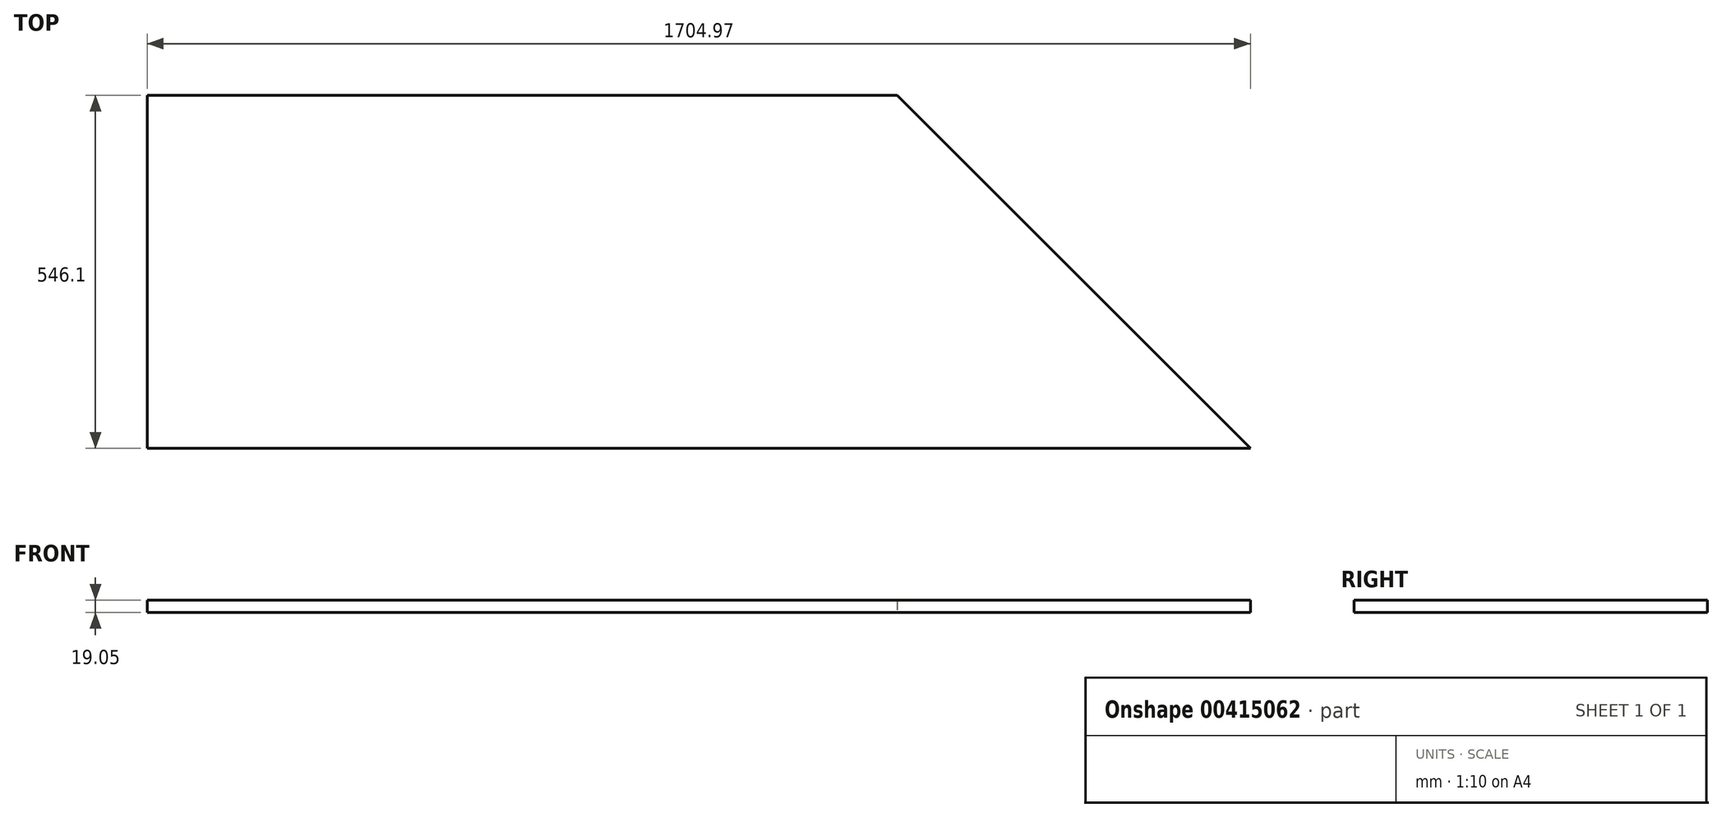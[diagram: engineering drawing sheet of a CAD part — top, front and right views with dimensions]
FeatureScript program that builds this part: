
annotation { "Feature Type Name" : "Feature", "Feature Type Description" : "" }
export const myFeature = defineFeature(function(context is Context, id is Id, definition is map)
    precondition{}
    {
        {
            var Q0;
            Q0=qCreatedBy(makeId("Top.planeOp"),FACE);
            var sketch = newSketch(context, id + "F0", { "sketchPlane" : qUnion([Q0])});
            skLineSegment(sketch, "E0", {"start": v(0, 0) * mm, "end": v(1704.98, 0) * mm});
            skLineSegment(sketch, "E1", {"start": v(1704.98, 0) * mm, "end": v(1158.88, 546.1) * mm});
            skLineSegment(sketch, "E2", {"start": v(1158.88, 546.1) * mm, "end": v(0, 546.1) * mm});
            skLineSegment(sketch, "E3", {"start": v(0, 546.1) * mm, "end": v(0, 0) * mm});
            skSolve(sketch);
        }
        {
            var Q0;
            Q0=makeQuery(id+"F0.imprint","IMPRINT",FACE,{"disambiguationData":[TD([[makeQuery(id+"F0.imprint","IMPRINT",EDGE,{"derivedFrom":sQuery(id+"F0.wireOp",EDGE,"E0")}),1.0]])]});
            extrude(context, id + "F1", {"entities" : qUnion([Q0]), "depth" : 19.05 * mm, "offsetDistance" : 25.4 * mm});
        }
    });
